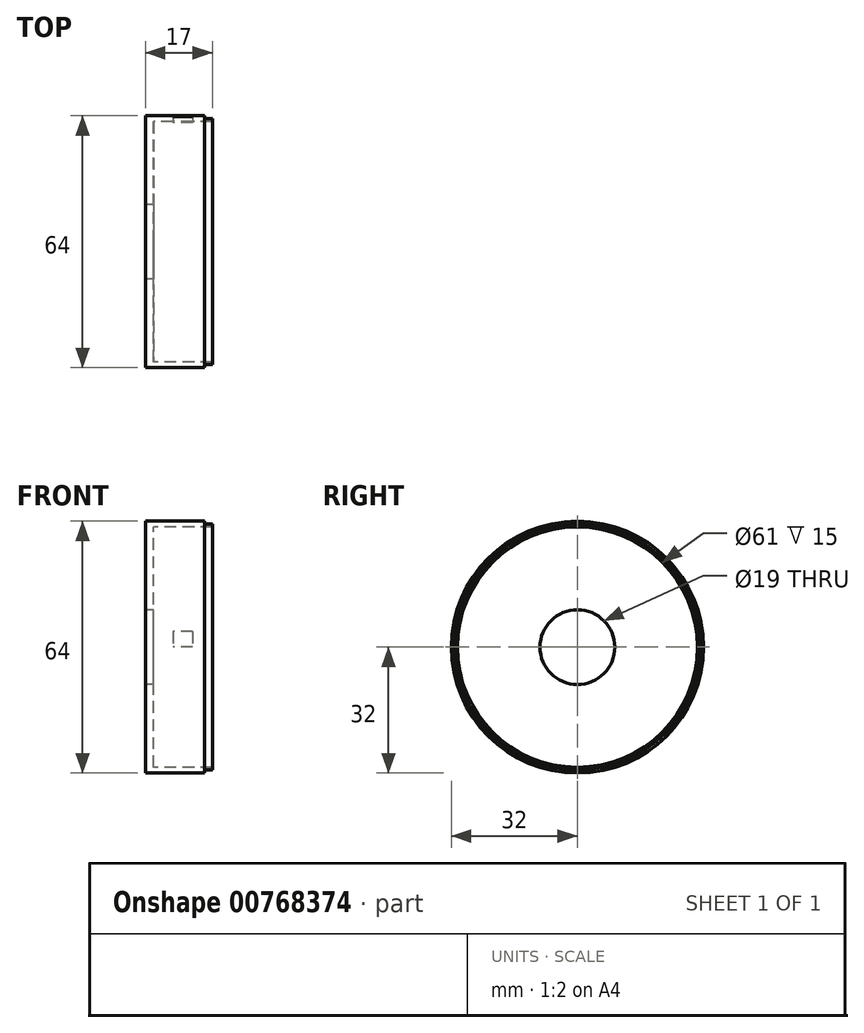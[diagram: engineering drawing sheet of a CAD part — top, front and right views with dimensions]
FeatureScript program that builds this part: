
annotation { "Feature Type Name" : "Feature", "Feature Type Description" : "" }
export const myFeature = defineFeature(function(context is Context, id is Id, definition is map)
    precondition{}
    {
        {
            var Q0;
            Q0=qCreatedBy(makeId("Right.planeOp"),FACE);
            var sketch = newSketch(context, id + "F0", { "sketchPlane" : qUnion([Q0])});
            skCircle(sketch, "E0", {"center": v(0, 0) * mm, "radius": 9.5 * mm});
            skCircle(sketch, "E1", {"center": v(0, 0) * mm, "radius": 30.5 * mm});
            skSolve(sketch);
        }
        {
            var Q0;
            Q0=makeQuery(id+"F0.imprint","IMPRINT",FACE,{"disambiguationData":[TD([[makeQuery(id+"F0.imprint","IMPRINT",EDGE,{"derivedFrom":sQuery(id+"F0.wireOp",EDGE,"E0")}),-1.0]])]});
            extrude(context, id + "F1", {"entities" : qUnion([Q0]), "depth" : 2 * mm, "offsetDistance" : 25 * mm});
        }
        {
            var Q0;
            Q0=makeQuery(id+"F1.opExtrude","CAP_FACE",FACE,{"disambiguationData":[OSD([sQuery(id+"F0.wireOp",EDGE,"E0"),sQuery(id+"F0.wireOp",EDGE,"E1")])],"isStart":true});
            var sketch = newSketch(context, id + "F2", { "sketchPlane" : qUnion([Q0])});
            skCircle(sketch, "E2", {"center": v(0, 0) * mm, "radius": 32 * mm});
            skSolve(sketch);
        }
        {
            var Q0;
            Q0=makeQuery(id+"F2.imprint","IMPRINT",FACE,{"disambiguationData":[TD([[makeQuery(id+"F2.imprint","IMPRINT",EDGE,{"derivedFrom":sQuery(id+"F2.wireOp",EDGE,"E2")}),1.0]])]});
            extrude(context, id + "F3", {"entities" : qUnion([Q0]), "operationType" : NewBodyOperationType.ADD, "oppositeDirection" : true, "depth" : 15 * mm, "offsetDistance" : 25 * mm});
        }
        {
            var Q0;
            {var subQ0=sQuery(id+"FSkdNozIkrlVV9G_1.wireOp",EDGE,"tOF25nVZ-zA19-Urb0-wr4W-roWmUhGncP15");var subQ1=sQuery(id+"FSkdNozIkrlVV9G_1.wireOp",EDGE,"L7OLgXmh-8isU-VI7p-XR34-cur48e1bNTiE");var subQ2=sQuery(id+"FSkdNozIkrlVV9G_1.wireOp",EDGE,"N4dev21w-GaUe-HBJV-lw8Q-oMCxEQS9QS8S");var subQ3=sQuery(id+"FSkdNozIkrlVV9G_1.wireOp",EDGE,"64UqEXOq-HEQ1-As1j-iaua-6nWA0H2MQHSX");var subQ4=sQuery(id+"F2.wireOp",EDGE,"E2");Q0=makeQuery(id+"Fr0dW6N1lpY9r39_1.2.FjaS6FO22Tx9eqM_1.boolean.opBoolean","MERGE",FACE,{"derivedFrom":[makeQuery(id+"Fr0dW6N1lpY9r39_1.1.FjaS6FO22Tx9eqM_1.boolean.opBoolean","MERGE",FACE,{"derivedFrom":[makeQuery(id+"FjaS6FO22Tx9eqM_1.boolean.opBoolean","MERGE",FACE,{"derivedFrom":[makeQuery(id+"F3.opExtrude","CAP_FACE",FACE,{"disambiguationData":[OSD([sQuery(id+"F0.wireOp",EDGE,"E1"),subQ4])],"isStart":false}),makeQuery(id+"FjaS6FO22Tx9eqM_1.opExtrude","CAP_FACE",FACE,{"disambiguationData":[OSD([subQ4,subQ3,subQ2,subQ1,subQ0])],"isStart":false})]}),makeQuery(id+"Fr0dW6N1lpY9r39_1.1.FjaS6FO22Tx9eqM_1.opExtrude","CAP_FACE",FACE,{"disambiguationData":[OSD([subQ4,subQ3,subQ2,subQ1,subQ0])],"isStart":false})]}),makeQuery(id+"Fr0dW6N1lpY9r39_1.2.FjaS6FO22Tx9eqM_1.opExtrude","CAP_FACE",FACE,{"disambiguationData":[OSD([subQ4,subQ3,subQ2,subQ1,subQ0])],"isStart":false})]});}
            var sketch = newSketch(context, id + "F4", { "sketchPlane" : qUnion([Q0])});
            skCircle(sketch, "E3", {"center": v(0, 0) * mm, "radius": 31.25 * mm});
            skSolve(sketch);
        }
        {
            var Q0;
            Q0=makeQuery(id+"F4.imprint","IMPRINT",FACE,{"disambiguationData":[TD([[makeQuery(id+"F4.imprint","IMPRINT",EDGE,{"derivedFrom":sQuery(id+"F4.wireOp",EDGE,"E3")}),1.0]])]});
            extrude(context, id + "F5", {"entities" : qUnion([Q0]), "operationType" : NewBodyOperationType.ADD, "depth" : 2 * mm, "offsetDistance" : 25 * mm});
        }
        {
            var Q0;
            Q0=qCreatedBy(makeId("Front.planeOp"),FACE);
            var sketch = newSketch(context, id + "F6", { "sketchPlane" : qUnion([Q0])});
            skLineSegment(sketch, "E4.bottom", {"start": v(7, 0) * mm, "end": v(12, 0) * mm});
            skLineSegment(sketch, "E4.top", {"start": v(7, 4) * mm, "end": v(12, 4) * mm});
            skLineSegment(sketch, "E4.left", {"start": v(12, 4) * mm, "end": v(12, 0) * mm});
            skLineSegment(sketch, "E4.right", {"start": v(7, 4) * mm, "end": v(7, 0) * mm});
            skSolve(sketch);
        }
        {
            var Q0;
            Q0=makeQuery(id+"F6.imprint","IMPRINT",FACE,{"disambiguationData":[TD([[makeQuery(id+"F6.imprint","IMPRINT",EDGE,{"derivedFrom":sQuery(id+"F6.wireOp",EDGE,"E4.bottom")}),1.0]])]});
            extrude(context, id + "F7", {"entities" : qUnion([Q0]), "operationType" : NewBodyOperationType.REMOVE, "oppositeDirection" : true, "depth" : 37.8 * mm, "offsetDistance" : 25 * mm});
        }
    });
